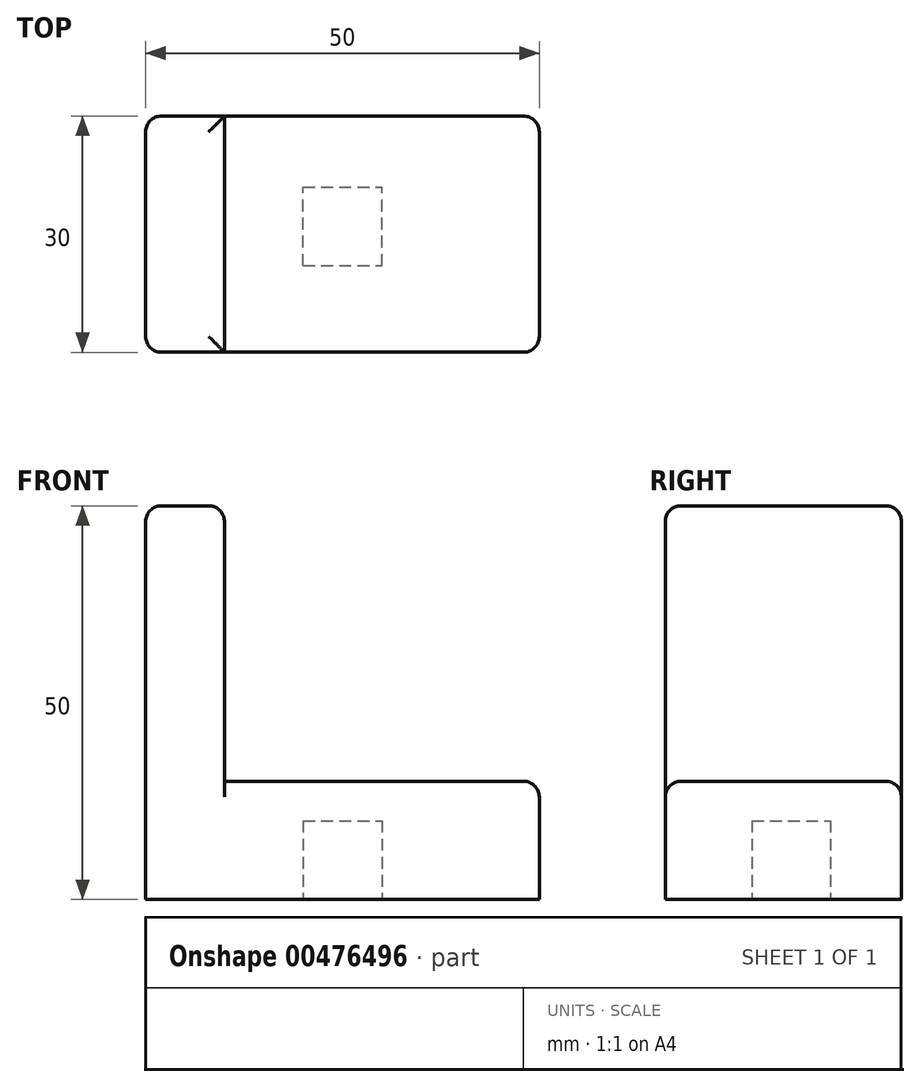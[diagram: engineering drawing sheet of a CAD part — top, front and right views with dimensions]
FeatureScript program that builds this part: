
annotation { "Feature Type Name" : "Feature", "Feature Type Description" : "" }
export const myFeature = defineFeature(function(context is Context, id is Id, definition is map)
    precondition{}
    {
        {
            var Q0;
            Q0=qCreatedBy(makeId("Top.planeOp"),FACE);
            var sketch = newSketch(context, id + "F0", { "sketchPlane" : qUnion([Q0])});
            skLineSegment(sketch, "E0.bottom", {"start": v(-24, 17.21) * mm, "end": v(26, 17.21) * mm});
            skLineSegment(sketch, "E0.top", {"start": v(-24, -12.79) * mm, "end": v(26, -12.79) * mm});
            skLineSegment(sketch, "E0.left", {"start": v(-24, 17.21) * mm, "end": v(-24, -12.79) * mm});
            skLineSegment(sketch, "E0.right", {"start": v(26, 17.21) * mm, "end": v(26, -12.79) * mm});
            skLineSegment(sketch, "E1", {"start": v(-14, -12.79) * mm, "end": v(-14, 17.21) * mm});
            skSolve(sketch);
        }
        {
            var Q0;
            {var subQ0=sQuery(id+"F0.wireOp",EDGE,"E0.right");Q0=makeQuery(id+"F0.imprint","IMPRINT",FACE,{"disambiguationData":[TD([[makeQuery(id+"F0.imprint","IMPRINT",EDGE,{"derivedFrom":subQ0}),-1.0]])]});}
            extrude(context, id + "F1", {"entities" : qUnion([Q0]), "depth" : 15 * mm});
        }
        {
            var Q0;
            {var subQ0=sQuery(id+"F0.wireOp",EDGE,"E0.left");Q0=makeQuery(id+"F0.imprint","IMPRINT",FACE,{"disambiguationData":[TD([[makeQuery(id+"F0.imprint","IMPRINT",EDGE,{"derivedFrom":subQ0}),1.0]])]});}
            extrude(context, id + "F2", {"entities" : qUnion([Q0]), "operationType" : NewBodyOperationType.ADD, "depth" : 50 * mm});
        }
        {
            var Q0;
            {var subQ0=sQuery(id+"F0.wireOp",EDGE,"E0.right");Q0=makeQuery(id+"F0.imprint","IMPRINT",FACE,{"disambiguationData":[TD([[makeQuery(id+"F0.imprint","IMPRINT",EDGE,{"derivedFrom":subQ0}),-1.0]])]});}
            var sketch = newSketch(context, id + "F3", { "sketchPlane" : qUnion([Q0])});
            skLineSegment(sketch, "E2.bottom", {"start": v(-4, -1.79) * mm, "end": v(6, -1.79) * mm});
            skLineSegment(sketch, "E2.top", {"start": v(-4, 8.21) * mm, "end": v(6, 8.21) * mm});
            skLineSegment(sketch, "E2.left", {"start": v(-4, -1.79) * mm, "end": v(-4, 8.21) * mm});
            skLineSegment(sketch, "E2.right", {"start": v(6, -1.79) * mm, "end": v(6, 8.21) * mm});
            skSolve(sketch);
        }
        {
            var Q0;
            Q0=makeQuery(id+"F3.imprint","IMPRINT",FACE,{"disambiguationData":[TD([[makeQuery(id+"F3.imprint","IMPRINT",EDGE,{"derivedFrom":sQuery(id+"F3.wireOp",EDGE,"E2.bottom")}),1.0]])]});
            extrude(context, id + "F4", {"entities" : qUnion([Q0]), "operationType" : NewBodyOperationType.REMOVE, "depth" : 10 * mm});
        }
        {
            var Q0;
            Q0=makeQuery(id+"F2.opExtrude","CAP_EDGE",EDGE,{"disambiguationData":[OSD([sQuery(id+"F0.wireOp",EDGE,"E0.top")])],"isStart":false});
            var Q1;
            Q1=makeQuery(id+"F2.opExtrude","CAP_EDGE",EDGE,{"disambiguationData":[OSD([sQuery(id+"F0.wireOp",EDGE,"E1")])],"isStart":false});
            var Q2;
            Q2=makeQuery(id+"F2.opExtrude","CAP_EDGE",EDGE,{"disambiguationData":[OSD([sQuery(id+"F0.wireOp",EDGE,"E0.left")])],"isStart":false});
            var Q3;
            Q3=makeQuery(id+"F2.opExtrude","CAP_EDGE",EDGE,{"disambiguationData":[OSD([sQuery(id+"F0.wireOp",EDGE,"E0.bottom")])],"isStart":false});
            var Q4;
            Q4=makeQuery(id+"F1.opExtrude","CAP_EDGE",EDGE,{"disambiguationData":[OSD([sQuery(id+"F0.wireOp",EDGE,"E0.top")])],"isStart":false});
            var Q5;
            Q5=makeQuery(id+"F1.opExtrude","CAP_EDGE",EDGE,{"disambiguationData":[OSD([sQuery(id+"F0.wireOp",EDGE,"E0.right")])],"isStart":false});
            var Q6;
            Q6=makeQuery(id+"F1.opExtrude","CAP_EDGE",EDGE,{"disambiguationData":[OSD([sQuery(id+"F0.wireOp",EDGE,"E0.bottom")])],"isStart":false});
            var Q7;
            Q7=makeQuery(id+"F1.opExtrude","SWEPT_EDGE",EDGE,{"disambiguationData":[OSD([sQuery(id+"F0.wireOp",EDGE,"E0.bottom"),sQuery(id+"F0.wireOp",EDGE,"E0.right")])]});
            var Q8;
            Q8=makeQuery(id+"F1.opExtrude","SWEPT_EDGE",EDGE,{"disambiguationData":[OSD([sQuery(id+"F0.wireOp",EDGE,"E0.top"),sQuery(id+"F0.wireOp",EDGE,"E0.right")])]});
            var Q9;
            Q9=makeQuery(id+"F2.opExtrude","SWEPT_EDGE",EDGE,{"disambiguationData":[OSD([sQuery(id+"F0.wireOp",EDGE,"E0.bottom"),sQuery(id+"F0.wireOp",EDGE,"E0.left")])]});
            var Q10;
            Q10=makeQuery(id+"F2.opExtrude","SWEPT_EDGE",EDGE,{"disambiguationData":[OSD([sQuery(id+"F0.wireOp",EDGE,"E0.top"),sQuery(id+"F0.wireOp",EDGE,"E0.left")])]});
            fillet(context, id + "F5", {"entities" : qUnion([Q0, Q1, Q2, Q3, Q4, Q5, Q6, Q7, Q8, Q9, Q10]), "radius" : 2 * mm, "tangentPropagation" : true, "allowEdgeOverflow" : false});
        }
    });
